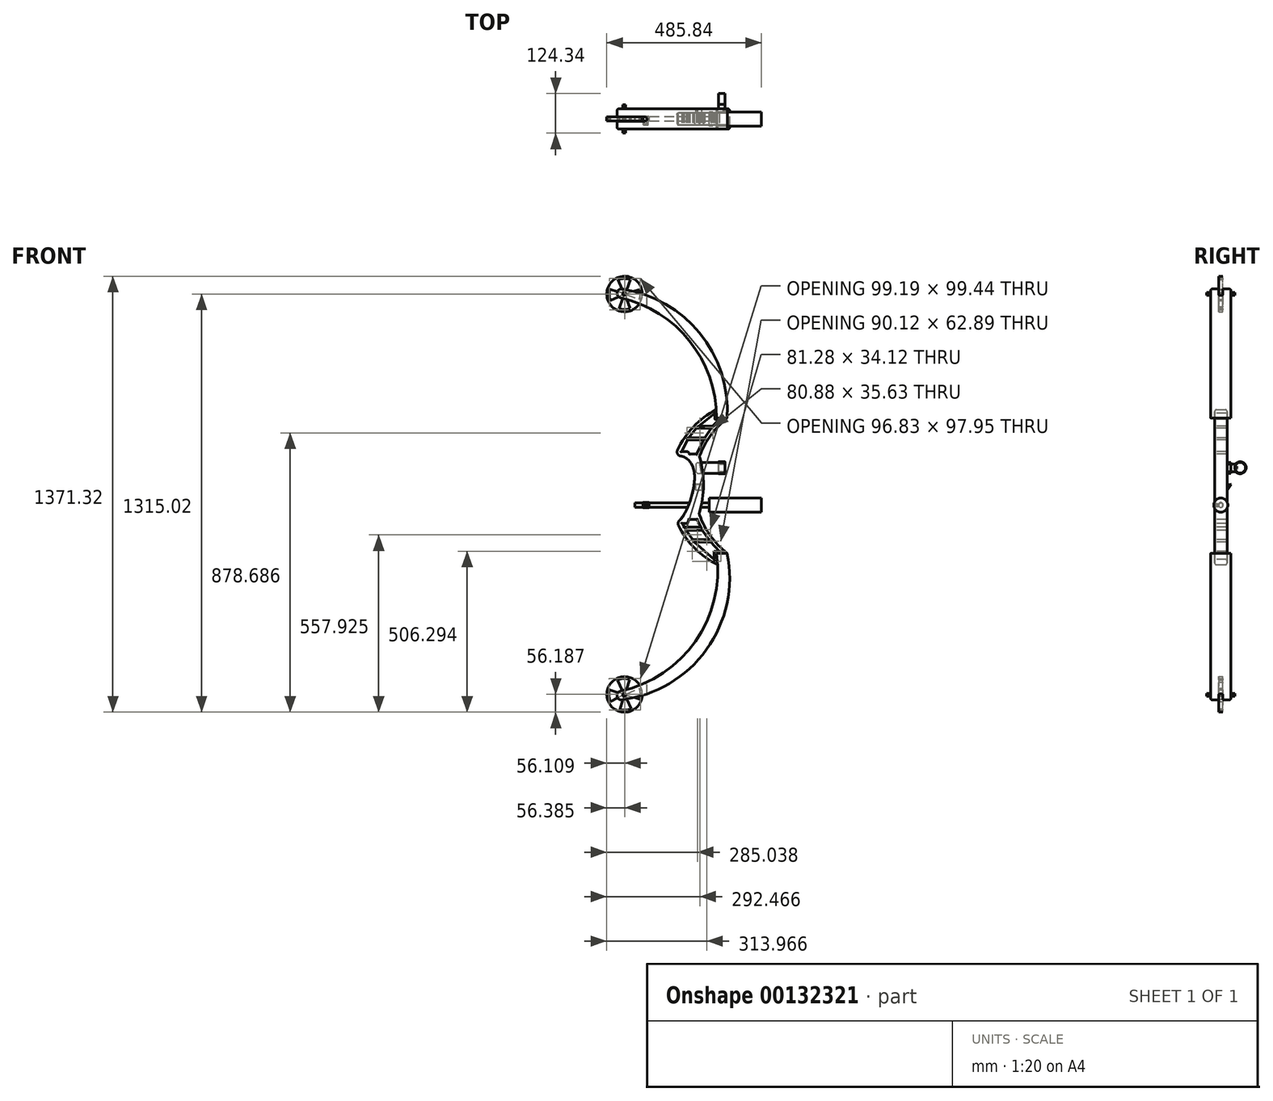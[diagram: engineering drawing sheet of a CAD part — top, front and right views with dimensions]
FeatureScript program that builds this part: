
annotation { "Feature Type Name" : "Feature", "Feature Type Description" : "" }
export const myFeature = defineFeature(function(context is Context, id is Id, definition is map)
    precondition{}
    {
        {
            var Q0;
            Q0=qCreatedBy(makeId("Front.planeOp"),FACE);
            var sketch = newSketch(context, id + "F0", { "sketchPlane" : qUnion([Q0])});
            skArc(sketch, "E0", {"start": v(312.15, 225.22) * mm, "mid": v(224.63, 471.96) * mm, "end": v(0, 606.44) * mm});
            skArc(sketch, "E1", {"start": v(0, -635.15) * mm, "mid": v(243.69, -480.2) * mm, "end": v(312.15, -199.65) * mm});
            skLineSegment(sketch, "E2", {"start": v(0, 606.44) * mm, "end": v(0, 633.37) * mm});
            skLineSegment(sketch, "E3", {"start": v(0, -635.15) * mm, "end": v(0, -662.07) * mm});
            skLineSegment(sketch, "E4", {"start": v(312.15, 225.22) * mm, "end": v(345.94, 225.22) * mm});
            skLineSegment(sketch, "E5", {"start": v(312.15, -199.65) * mm, "end": v(345.93, -199.65) * mm});
            skArc(sketch, "E6", {"start": v(345.94, 225.22) * mm, "mid": v(254.91, 498.75) * mm, "end": v(0, 633.37) * mm});
            skArc(sketch, "E7", {"start": v(0, -662.07) * mm, "mid": v(276.6, -508.4) * mm, "end": v(345.93, -199.65) * mm});
            skSolve(sketch);
        }
        {
            var Q0;
            Q0 = qSketchRegion(id + "F0", true);
            extrude(context, id + "F1", {"entities" : qUnion([Q0]), "depth" : 38.1 * mm, "hasSecondDirection" : true, "secondDirectionOppositeDirection" : true, "secondDirectionDepth" : 25.4 * mm});
        }
        {
            var Q0;
            Q0=qCreatedBy(makeId("Front.planeOp"),FACE);
            var sketch = newSketch(context, id + "F2", { "sketchPlane" : qUnion([Q0])});
            skArc(sketch, "E8", {"start": v(328.65, 260.2) * mm, "mid": v(164.15, 6.75) * mm, "end": v(333.35, -243.58) * mm});
            skArc(sketch, "E9", {"start": v(345.8, 225.54) * mm, "mid": v(242.77, 13.02) * mm, "end": v(345.76, -199.52) * mm});
            skLineSegment(sketch, "E10", {"start": v(333.35, -243.58) * mm, "end": v(345.76, -199.52) * mm});
            skLineSegment(sketch, "E11", {"start": v(328.65, 260.2) * mm, "end": v(345.8, 225.54) * mm});
            skArc(sketch, "E12", {"start": v(257.5, -75.1) * mm, "mid": v(271.65, 14.65) * mm, "end": v(258.73, 104.58) * mm});
            skArc(sketch, "E13", {"start": v(176.09, -70.66) * mm, "mid": v(193.2, 15.9) * mm, "end": v(180.78, 103.27) * mm});
            skSolve(sketch);
        }
        {
            var Q0;
            Q0 = qSketchRegion(id + "F2", true);
            extrude(context, id + "F3", {"entities" : qUnion([Q0]), "operationType" : NewBodyOperationType.ADD, "depth" : 25.4 * mm, "hasSecondDirection" : true, "secondDirectionOppositeDirection" : true, "secondDirectionDepth" : 13.4 * mm});
        }
        {
            var Q0;
            Q0 = qSketchRegion(id + "F2", true);
            extrude(context, id + "F4", {"entities" : qUnion([Q0]), "operationType" : NewBodyOperationType.ADD, "depth" : 25.4 * mm});
        }
        {
            var Q0;
            Q0=qCreatedBy(makeId("Front.planeOp"),FACE);
            var sketch = newSketch(context, id + "F5", { "sketchPlane" : qUnion([Q0])});
            skFitSpline(sketch, "E14", {"points": [v(182.57, 103.7) * mm, v(240.87, 63.55) * mm, v(188.22, -101.45) * mm, v(156.8, -24.45) * mm, v(182.57, 103.7) * mm]});
            skSolve(sketch);
        }
        {
            var Q0;
            Q0 = qSketchRegion(id + "F5", true);
            extrude(context, id + "F6", {"entities" : qUnion([Q0]), "operationType" : NewBodyOperationType.REMOVE, "oppositeDirection" : true, "depth" : 25.4 * mm, "hasSecondDirection" : true, "secondDirectionOppositeDirection" : false, "secondDirectionDepth" : 25.4 * mm});
        }
        {
            var Q0;
            {var subQ0=sQuery(id+"F2.wireOp",EDGE,"E8");Q0=makeQuery(id+"F6.boolean.opBoolean","INTERSECT",EDGE,{"disambiguationData":[OD(0.0)],"derivedFrom":[makeQuery(id+"F4.boolean.opBoolean","MERGE",FACE,{"derivedFrom":[makeQuery(id+"F3.opExtrude","SWEPT_FACE",FACE,{"disambiguationData":[OSD([subQ0])]}),makeQuery(id+"F4.opExtrude","SWEPT_FACE",FACE,{"disambiguationData":[OSD([subQ0])]})]}),makeQuery(id+"F6.opExtrude","SWEPT_FACE",FACE,{"disambiguationData":[OSD([sQuery(id+"F5.wireOp",EDGE,"E14")])]})]});}
            var Q1;
            {var subQ0=sQuery(id+"F2.wireOp",EDGE,"E8");Q1=makeQuery(id+"F6.boolean.opBoolean","INTERSECT",EDGE,{"disambiguationData":[OD(1.0)],"derivedFrom":[makeQuery(id+"F4.boolean.opBoolean","MERGE",FACE,{"derivedFrom":[makeQuery(id+"F3.opExtrude","SWEPT_FACE",FACE,{"disambiguationData":[OSD([subQ0])]}),makeQuery(id+"F4.opExtrude","SWEPT_FACE",FACE,{"disambiguationData":[OSD([subQ0])]})]}),makeQuery(id+"F6.opExtrude","SWEPT_FACE",FACE,{"disambiguationData":[OSD([sQuery(id+"F5.wireOp",EDGE,"E14")])]})]});}
            var Q2;
            {var subQ0=sQuery(id+"F2.wireOp",EDGE,"E12");var subQ1=sQuery(id+"F2.wireOp",EDGE,"E9");var subQ2=makeQuery(id+"F2.imprint","INTERSECT",VERTEX,{"disambiguationData":[OD(1.0)],"derivedFrom":[subQ1,subQ0]});Q2=makeQuery(id+"F4.boolean.opBoolean","MERGE",EDGE,{"derivedFrom":[makeQuery(id+"F3.opExtrude","SWEPT_EDGE",EDGE,{"disambiguationData":[OSD([subQ1,subQ0]),TDD([subQ2])]}),makeQuery(id+"F4.opExtrude","SWEPT_EDGE",EDGE,{"disambiguationData":[OSD([subQ1,subQ0]),TDD([subQ2])]})]});}
            var Q3;
            {var subQ0=sQuery(id+"F2.wireOp",EDGE,"E12");var subQ1=sQuery(id+"F2.wireOp",EDGE,"E9");var subQ2=makeQuery(id+"F2.imprint","INTERSECT",VERTEX,{"disambiguationData":[OD(0.0)],"derivedFrom":[subQ1,subQ0]});Q3=makeQuery(id+"F4.boolean.opBoolean","MERGE",EDGE,{"derivedFrom":[makeQuery(id+"F3.opExtrude","SWEPT_EDGE",EDGE,{"disambiguationData":[OSD([subQ1,subQ0]),TDD([subQ2])]}),makeQuery(id+"F4.opExtrude","SWEPT_EDGE",EDGE,{"disambiguationData":[OSD([subQ1,subQ0]),TDD([subQ2])]})]});}
            var Q4;
            Q4=makeQuery(id+"F1.opExtrude","SWEPT_EDGE",EDGE,{"disambiguationData":[OSD([sQuery(id+"F0.wireOp",EDGE,"E3"),sQuery(id+"F0.wireOp",EDGE,"E7")])]});
            var Q5;
            Q5=makeQuery(id+"F1.opExtrude","SWEPT_EDGE",EDGE,{"disambiguationData":[OSD([sQuery(id+"F0.wireOp",EDGE,"E1"),sQuery(id+"F0.wireOp",EDGE,"E3")])]});
            var Q6;
            Q6=makeQuery(id+"F1.opExtrude","SWEPT_EDGE",EDGE,{"disambiguationData":[OSD([sQuery(id+"F0.wireOp",EDGE,"E0"),sQuery(id+"F0.wireOp",EDGE,"E2")])]});
            var Q7;
            Q7=makeQuery(id+"F1.opExtrude","SWEPT_EDGE",EDGE,{"disambiguationData":[OSD([sQuery(id+"F0.wireOp",EDGE,"E2"),sQuery(id+"F0.wireOp",EDGE,"E6")])]});
            fillet(context, id + "F7", {"entities" : qUnion([Q0, Q1, Q2, Q3, Q4, Q5, Q6, Q7]), "radius" : 12.7 * mm, "tangentPropagation" : true, "allowEdgeOverflow" : false});
        }
        {
            var Q0;
            Q0=makeQuery(id+"F1.opExtrude","CAP_EDGE",EDGE,{"disambiguationData":[OSD([sQuery(id+"F0.wireOp",EDGE,"E0")])],"isStart":false});
            var Q1;
            Q1=makeQuery(id+"F1.opExtrude","CAP_EDGE",EDGE,{"disambiguationData":[OSD([sQuery(id+"F0.wireOp",EDGE,"E0")])],"isStart":true});
            var Q2;
            {var subQ0=sQuery(id+"F2.wireOp",EDGE,"E8");Q2=makeQuery(id+"F6.boolean.opBoolean","SPLIT",EDGE,{"disambiguationData":[TD([makeQuery(id+"F1.opExtrude","SWEPT_FACE",FACE,{"disambiguationData":[OSD([sQuery(id+"F0.wireOp",EDGE,"E0")])]})])],"derivedFrom":makeQuery(id+"F3.opExtrude","CAP_EDGE",EDGE,{"disambiguationData":[OSD([subQ0])],"isStart":true})});}
            var Q3;
            {var subQ0=sQuery(id+"F2.wireOp",EDGE,"E9");Q3=makeQuery(id+"F3.opExtrude","CAP_EDGE",EDGE,{"disambiguationData":[OSD([subQ0]),TDD([makeQuery(id+"F2.imprint","IMPRINT",EDGE,{"disambiguationData":[TD([[makeQuery(id+"F2.imprint","INTERSECT",VERTEX,{"derivedFrom":[subQ0,sQuery(id+"F2.wireOp",EDGE,"E11")]}),-1.0]])],"derivedFrom":subQ0})])],"isStart":true});}
            var Q4;
            {var subQ0=sQuery(id+"F2.wireOp",EDGE,"E8");Q4=makeQuery(id+"F6.boolean.opBoolean","SPLIT",EDGE,{"disambiguationData":[TD([makeQuery(id+"F1.opExtrude","SWEPT_FACE",FACE,{"disambiguationData":[OSD([sQuery(id+"F0.wireOp",EDGE,"E0")])]})])],"derivedFrom":makeQuery(id+"F3.opExtrude","CAP_EDGE",EDGE,{"disambiguationData":[OSD([subQ0])],"isStart":false})});}
            var Q5;
            {var subQ0=sQuery(id+"F2.wireOp",EDGE,"E9");Q5=makeQuery(id+"F3.opExtrude","CAP_EDGE",EDGE,{"disambiguationData":[OSD([subQ0]),TDD([makeQuery(id+"F2.imprint","IMPRINT",EDGE,{"disambiguationData":[TD([[makeQuery(id+"F2.imprint","INTERSECT",VERTEX,{"derivedFrom":[subQ0,sQuery(id+"F2.wireOp",EDGE,"E11")]}),-1.0]])],"derivedFrom":subQ0})])],"isStart":false});}
            var Q6;
            Q6=makeQuery(id+"F1.opExtrude","CAP_EDGE",EDGE,{"disambiguationData":[OSD([sQuery(id+"F0.wireOp",EDGE,"E1")])],"isStart":true});
            var Q7;
            Q7=makeQuery(id+"F1.opExtrude","CAP_EDGE",EDGE,{"disambiguationData":[OSD([sQuery(id+"F0.wireOp",EDGE,"E1")])],"isStart":false});
            fillet(context, id + "F8", {"entities" : qUnion([Q0, Q1, Q2, Q3, Q4, Q5, Q6, Q7]), "radius" : 5.08 * mm, "tangentPropagation" : true, "allowEdgeOverflow" : false});
        }
        {
            var Q0;
            Q0=qCreatedBy(makeId("Top.planeOp"),FACE);
            var sketch = newSketch(context, id + "F9", { "sketchPlane" : qUnion([Q0])});
            skLineSegment(sketch, "E15", {"start": v(0, 0) * mm, "end": v(87.64, 0) * mm});
            skLineSegment(sketch, "E16", {"start": v(0, -12.95) * mm, "end": v(87.64, -12.95) * mm});
            skArc(sketch, "E17", {"start": v(87.64, -12.95) * mm, "mid": v(94.11, -6.48) * mm, "end": v(87.64, 0) * mm});
            skLineSegment(sketch, "E18", {"start": v(0, 0) * mm, "end": v(0, -12.95) * mm});
            skSolve(sketch);
        }
        {
            var Q0;
            Q0 = qSketchRegion(id + "F9", true);
            extrude(context, id + "F10", {"entities" : qUnion([Q0]), "operationType" : NewBodyOperationType.REMOVE, "oppositeDirection" : true, "depth" : 1043.23 * mm, "hasSecondDirection" : true, "secondDirectionOppositeDirection" : false, "secondDirectionDepth" : 725.43 * mm});
        }
        {
            var Q0;
            Q0=qCreatedBy(makeId("Front.planeOp"),FACE);
            var sketch = newSketch(context, id + "F11", { "sketchPlane" : qUnion([Q0])});
            skLineSegment(sketch, "E19", {"start": v(307.3, 240.65) * mm, "end": v(307.3, 221.5) * mm});
            skLineSegment(sketch, "E20", {"start": v(307.3, 221.5) * mm, "end": v(321.6, 221.5) * mm});
            skLineSegment(sketch, "E21", {"start": v(321.6, 221.5) * mm, "end": v(299.17, 200.17) * mm});
            skLineSegment(sketch, "E22", {"start": v(299.17, 200.17) * mm, "end": v(257.15, 200.17) * mm});
            skLineSegment(sketch, "E23", {"start": v(257.15, 200.17) * mm, "end": v(307.3, 240.65) * mm});
            skLineSegment(sketch, "E24", {"start": v(249.41, 194.56) * mm, "end": v(295.62, 194.56) * mm});
            skLineSegment(sketch, "E25", {"start": v(295.62, 194.56) * mm, "end": v(275.44, 164.01) * mm});
            skLineSegment(sketch, "E26", {"start": v(275.44, 164.01) * mm, "end": v(224.78, 164.01) * mm});
            skLineSegment(sketch, "E27", {"start": v(224.78, 164.01) * mm, "end": v(249.41, 194.56) * mm});
            skLineSegment(sketch, "E28", {"start": v(221.45, 157.23) * mm, "end": v(202.6, 120.92) * mm});
            skLineSegment(sketch, "E29", {"start": v(202.6, 120.92) * mm, "end": v(222.32, 120.92) * mm});
            skLineSegment(sketch, "E30", {"start": v(222.32, 120.92) * mm, "end": v(228.43, 112.54) * mm});
            skLineSegment(sketch, "E31", {"start": v(228.43, 112.54) * mm, "end": v(249.56, 112.54) * mm});
            skLineSegment(sketch, "E32", {"start": v(249.56, 112.54) * mm, "end": v(272.08, 156.7) * mm});
            skLineSegment(sketch, "E33", {"start": v(272.08, 156.7) * mm, "end": v(221.45, 157.23) * mm});
            skSolve(sketch);
        }
        {
            var Q0;
            Q0 = qSketchRegion(id + "F11", true);
            extrude(context, id + "F12", {"entities" : qUnion([Q0]), "operationType" : NewBodyOperationType.REMOVE, "oppositeDirection" : true, "depth" : 25.4 * mm, "hasSecondDirection" : true, "secondDirectionOppositeDirection" : false, "secondDirectionDepth" : 103.34 * mm});
        }
        {
            var Q0;
            Q0=qCreatedBy(makeId("Front.planeOp"),FACE);
            var sketch = newSketch(context, id + "F13", { "sketchPlane" : qUnion([Q0])});
            skLineSegment(sketch, "E34", {"start": v(304.9, -218.91) * mm, "end": v(304.9, -193.2) * mm});
            skLineSegment(sketch, "E35", {"start": v(304.9, -193.2) * mm, "end": v(320.72, -193.2) * mm});
            skLineSegment(sketch, "E36", {"start": v(320.72, -193.2) * mm, "end": v(294.36, -164.2) * mm});
            skLineSegment(sketch, "E37", {"start": v(294.36, -164.2) * mm, "end": v(243.05, -164.2) * mm});
            skLineSegment(sketch, "E38", {"start": v(243.05, -164.2) * mm, "end": v(304.9, -218.91) * mm});
            skLineSegment(sketch, "E39", {"start": v(288.23, -156) * mm, "end": v(237.22, -156) * mm});
            skLineSegment(sketch, "E40", {"start": v(237.22, -156) * mm, "end": v(216.74, -126.96) * mm});
            skLineSegment(sketch, "E41", {"start": v(216.74, -126.96) * mm, "end": v(267.82, -126.96) * mm});
            skLineSegment(sketch, "E42", {"start": v(267.82, -126.96) * mm, "end": v(288.23, -156) * mm});
            skLineSegment(sketch, "E43", {"start": v(262.27, -117.14) * mm, "end": v(210.93, -117.14) * mm});
            skLineSegment(sketch, "E44", {"start": v(210.93, -117.14) * mm, "end": v(205.44, -106.16) * mm});
            skLineSegment(sketch, "E45", {"start": v(205.44, -106.16) * mm, "end": v(220.33, -106.16) * mm});
            skLineSegment(sketch, "E46", {"start": v(220.33, -106.16) * mm, "end": v(226.6, -93.23) * mm});
            skLineSegment(sketch, "E47", {"start": v(226.6, -93.23) * mm, "end": v(251.3, -93.23) * mm});
            skLineSegment(sketch, "E48", {"start": v(251.3, -93.23) * mm, "end": v(262.27, -117.14) * mm});
            skSolve(sketch);
        }
        {
            var Q0;
            Q0 = qSketchRegion(id + "F13", true);
            extrude(context, id + "F14", {"entities" : qUnion([Q0]), "operationType" : NewBodyOperationType.REMOVE, "oppositeDirection" : true, "depth" : 25.4 * mm, "hasSecondDirection" : true, "secondDirectionOppositeDirection" : false, "secondDirectionDepth" : 136.26 * mm});
        }
        {
            var Q0;
            Q0=qCreatedBy(makeId("Front.planeOp"),FACE);
            var sketch = newSketch(context, id + "F15", { "sketchPlane" : qUnion([Q0])});
            skCircle(sketch, "E49", {"center": v(23.33, 616.03) * mm, "radius": 55.9 * mm});
            skCircle(sketch, "E50", {"center": v(23.33, -643.5) * mm, "radius": 55.9 * mm});
            skCircle(sketch, "E51", {"center": v(23.33, 616.03) * mm, "radius": 4.58 * mm});
            skLineSegment(sketch, "E52", {"start": v(19.88, 619.04) * mm, "end": v(2.06, 661.07) * mm});
            skLineSegment(sketch, "E53", {"start": v(26.37, 619.46) * mm, "end": v(42.28, 661.63) * mm});
            skLineSegment(sketch, "E54", {"start": v(20.5, 612.42) * mm, "end": v(6.51, 570.45) * mm});
            skLineSegment(sketch, "E55", {"start": v(26.38, 612.6) * mm, "end": v(40.24, 570.82) * mm});
            skArc(sketch, "E56", {"start": v(42.28, 661.63) * mm, "mid": v(22.13, 664.6) * mm, "end": v(2.06, 661.07) * mm});
            skArc(sketch, "E57", {"start": v(6.51, 570.45) * mm, "mid": v(23.42, 566.64) * mm, "end": v(40.24, 570.82) * mm});
            skLineSegment(sketch, "E58", {"start": v(27.5, 617.94) * mm, "end": v(69.87, 630.2) * mm});
            skLineSegment(sketch, "E59", {"start": v(27.5, 614.11) * mm, "end": v(69.21, 598.67) * mm});
            skLineSegment(sketch, "E60", {"start": v(19.14, 617.87) * mm, "end": v(-22.68, 630.88) * mm});
            skLineSegment(sketch, "E61", {"start": v(19.1, 614.26) * mm, "end": v(-21.29, 595.17) * mm});
            skArc(sketch, "E62", {"start": v(-22.68, 630.88) * mm, "mid": v(-24.57, 612.92) * mm, "end": v(-21.29, 595.17) * mm});
            skArc(sketch, "E63", {"start": v(69.21, 598.67) * mm, "mid": v(72.24, 614.38) * mm, "end": v(69.87, 630.2) * mm});
            skCircle(sketch, "E64", {"center": v(23.33, -643.5) * mm, "radius": 4.58 * mm});
            skLineSegment(sketch, "E65", {"start": v(20.29, -640.08) * mm, "end": v(1.41, -598.57) * mm});
            skLineSegment(sketch, "E66", {"start": v(25.93, -639.73) * mm, "end": v(39.75, -596.96) * mm});
            skLineSegment(sketch, "E67", {"start": v(21.54, -647.73) * mm, "end": v(8.9, -690.96) * mm});
            skLineSegment(sketch, "E68", {"start": v(26, -647.23) * mm, "end": v(44, -688.73) * mm});
            skLineSegment(sketch, "E69", {"start": v(27.8, -642.46) * mm, "end": v(69.69, -624.26) * mm});
            skLineSegment(sketch, "E70", {"start": v(27.47, -645.49) * mm, "end": v(70.34, -658.33) * mm});
            skLineSegment(sketch, "E71", {"start": v(18.96, -642.13) * mm, "end": v(-24.47, -629.13) * mm});
            skLineSegment(sketch, "E72", {"start": v(19.17, -645.42) * mm, "end": v(-19.95, -665.33) * mm});
            skArc(sketch, "E73", {"start": v(39.75, -596.96) * mm, "mid": v(20.4, -593.5) * mm, "end": v(1.41, -598.57) * mm});
            skArc(sketch, "E74", {"start": v(-24.47, -629.13) * mm, "mid": v(-25.69, -647.66) * mm, "end": v(-19.95, -665.33) * mm});
            skArc(sketch, "E75", {"start": v(8.9, -690.96) * mm, "mid": v(26.64, -692.84) * mm, "end": v(44, -688.73) * mm});
            skArc(sketch, "E76", {"start": v(70.34, -658.33) * mm, "mid": v(73.15, -641.24) * mm, "end": v(69.69, -624.26) * mm});
            skSolve(sketch);
        }
        {
            var Q0;
            Q0=qCreatedBy(makeId("Front.planeOp"),FACE);
            var sketch = newSketch(context, id + "F16", { "sketchPlane" : qUnion([Q0])});
            skCircle(sketch, "E77", {"center": v(21.85, 616.5) * mm, "radius": 4.59 * mm});
            skCircle(sketch, "E78", {"center": v(21.85, -645.2) * mm, "radius": 4.58 * mm});
            skSolve(sketch);
        }
        {
            var Q0;
            Q0 = qSketchRegion(id + "F16", true);
            extrude(context, id + "F17", {"entities" : qUnion([Q0]), "operationType" : NewBodyOperationType.ADD, "depth" : 50.8 * mm, "hasSecondDirection" : true, "secondDirectionOppositeDirection" : true, "secondDirectionDepth" : 38.1 * mm});
        }
        {
            var Q0;
            Q0 = qSketchRegion(id + "F15", true);
            extrude(context, id + "F18", {"entities" : qUnion([Q0]), "depth" : 12.7 * mm});
        }
        {
            var Q0;
            Q0=makeQuery(id+"F12.boolean.opBoolean","INTERSECT",EDGE,{"derivedFrom":[makeQuery(id+"F3.opExtrude","CAP_FACE",FACE,{"disambiguationData":[OSD([sQuery(id+"F2.wireOp",EDGE,"E8"),sQuery(id+"F2.wireOp",EDGE,"E9"),sQuery(id+"F2.wireOp",EDGE,"E10"),sQuery(id+"F2.wireOp",EDGE,"E11"),sQuery(id+"F2.wireOp",EDGE,"E12")])],"isStart":false}),makeQuery(id+"F12.opExtrude","SWEPT_FACE",FACE,{"disambiguationData":[OSD([sQuery(id+"F11.wireOp",EDGE,"E26")])]})]});
            var Q1;
            Q1=makeQuery(id+"F12.boolean.opBoolean","INTERSECT",EDGE,{"derivedFrom":[makeQuery(id+"F3.opExtrude","CAP_FACE",FACE,{"disambiguationData":[OSD([sQuery(id+"F2.wireOp",EDGE,"E8"),sQuery(id+"F2.wireOp",EDGE,"E9"),sQuery(id+"F2.wireOp",EDGE,"E10"),sQuery(id+"F2.wireOp",EDGE,"E11"),sQuery(id+"F2.wireOp",EDGE,"E12")])],"isStart":false}),makeQuery(id+"F12.opExtrude","SWEPT_FACE",FACE,{"disambiguationData":[OSD([sQuery(id+"F11.wireOp",EDGE,"E31")])]})]});
            var Q2;
            Q2=makeQuery(id+"F12.boolean.opBoolean","INTERSECT",EDGE,{"derivedFrom":[makeQuery(id+"F3.opExtrude","CAP_FACE",FACE,{"disambiguationData":[OSD([sQuery(id+"F2.wireOp",EDGE,"E8"),sQuery(id+"F2.wireOp",EDGE,"E9"),sQuery(id+"F2.wireOp",EDGE,"E10"),sQuery(id+"F2.wireOp",EDGE,"E11"),sQuery(id+"F2.wireOp",EDGE,"E12")])],"isStart":false}),makeQuery(id+"F12.opExtrude","SWEPT_FACE",FACE,{"disambiguationData":[OSD([sQuery(id+"F11.wireOp",EDGE,"E30")])]})]});
            var Q3;
            Q3=makeQuery(id+"F12.boolean.opBoolean","INTERSECT",EDGE,{"derivedFrom":[makeQuery(id+"F3.opExtrude","CAP_FACE",FACE,{"disambiguationData":[OSD([sQuery(id+"F2.wireOp",EDGE,"E8"),sQuery(id+"F2.wireOp",EDGE,"E9"),sQuery(id+"F2.wireOp",EDGE,"E10"),sQuery(id+"F2.wireOp",EDGE,"E11"),sQuery(id+"F2.wireOp",EDGE,"E12")])],"isStart":false}),makeQuery(id+"F12.opExtrude","SWEPT_FACE",FACE,{"disambiguationData":[OSD([sQuery(id+"F11.wireOp",EDGE,"E29")])]})]});
            var Q4;
            Q4=makeQuery(id+"F12.boolean.opBoolean","INTERSECT",EDGE,{"derivedFrom":[makeQuery(id+"F3.opExtrude","CAP_FACE",FACE,{"disambiguationData":[OSD([sQuery(id+"F2.wireOp",EDGE,"E8"),sQuery(id+"F2.wireOp",EDGE,"E9"),sQuery(id+"F2.wireOp",EDGE,"E10"),sQuery(id+"F2.wireOp",EDGE,"E11"),sQuery(id+"F2.wireOp",EDGE,"E12")])],"isStart":false}),makeQuery(id+"F12.opExtrude","SWEPT_FACE",FACE,{"disambiguationData":[OSD([sQuery(id+"F11.wireOp",EDGE,"E32")])]})]});
            var Q5;
            Q5=makeQuery(id+"F12.boolean.opBoolean","INTERSECT",EDGE,{"derivedFrom":[makeQuery(id+"F3.opExtrude","CAP_FACE",FACE,{"disambiguationData":[OSD([sQuery(id+"F2.wireOp",EDGE,"E8"),sQuery(id+"F2.wireOp",EDGE,"E9"),sQuery(id+"F2.wireOp",EDGE,"E10"),sQuery(id+"F2.wireOp",EDGE,"E11"),sQuery(id+"F2.wireOp",EDGE,"E12")])],"isStart":false}),makeQuery(id+"F12.opExtrude","SWEPT_FACE",FACE,{"disambiguationData":[OSD([sQuery(id+"F11.wireOp",EDGE,"E33")])]})]});
            var Q6;
            Q6=makeQuery(id+"F12.boolean.opBoolean","INTERSECT",EDGE,{"derivedFrom":[makeQuery(id+"F3.opExtrude","CAP_FACE",FACE,{"disambiguationData":[OSD([sQuery(id+"F2.wireOp",EDGE,"E8"),sQuery(id+"F2.wireOp",EDGE,"E9"),sQuery(id+"F2.wireOp",EDGE,"E10"),sQuery(id+"F2.wireOp",EDGE,"E11"),sQuery(id+"F2.wireOp",EDGE,"E12")])],"isStart":false}),makeQuery(id+"F12.opExtrude","SWEPT_FACE",FACE,{"disambiguationData":[OSD([sQuery(id+"F11.wireOp",EDGE,"E28")])]})]});
            var Q7;
            Q7=makeQuery(id+"F12.boolean.opBoolean","INTERSECT",EDGE,{"derivedFrom":[makeQuery(id+"F3.opExtrude","CAP_FACE",FACE,{"disambiguationData":[OSD([sQuery(id+"F2.wireOp",EDGE,"E8"),sQuery(id+"F2.wireOp",EDGE,"E9"),sQuery(id+"F2.wireOp",EDGE,"E10"),sQuery(id+"F2.wireOp",EDGE,"E11"),sQuery(id+"F2.wireOp",EDGE,"E12")])],"isStart":false}),makeQuery(id+"F12.opExtrude","SWEPT_FACE",FACE,{"disambiguationData":[OSD([sQuery(id+"F11.wireOp",EDGE,"E25")])]})]});
            var Q8;
            Q8=makeQuery(id+"F12.boolean.opBoolean","INTERSECT",EDGE,{"derivedFrom":[makeQuery(id+"F3.opExtrude","CAP_FACE",FACE,{"disambiguationData":[OSD([sQuery(id+"F2.wireOp",EDGE,"E8"),sQuery(id+"F2.wireOp",EDGE,"E9"),sQuery(id+"F2.wireOp",EDGE,"E10"),sQuery(id+"F2.wireOp",EDGE,"E11"),sQuery(id+"F2.wireOp",EDGE,"E12")])],"isStart":false}),makeQuery(id+"F12.opExtrude","SWEPT_FACE",FACE,{"disambiguationData":[OSD([sQuery(id+"F11.wireOp",EDGE,"E24")])]})]});
            var Q9;
            Q9=makeQuery(id+"F12.boolean.opBoolean","INTERSECT",EDGE,{"derivedFrom":[makeQuery(id+"F3.opExtrude","CAP_FACE",FACE,{"disambiguationData":[OSD([sQuery(id+"F2.wireOp",EDGE,"E8"),sQuery(id+"F2.wireOp",EDGE,"E9"),sQuery(id+"F2.wireOp",EDGE,"E10"),sQuery(id+"F2.wireOp",EDGE,"E11"),sQuery(id+"F2.wireOp",EDGE,"E12")])],"isStart":false}),makeQuery(id+"F12.opExtrude","SWEPT_FACE",FACE,{"disambiguationData":[OSD([sQuery(id+"F11.wireOp",EDGE,"E27")])]})]});
            var Q10;
            Q10=makeQuery(id+"F12.boolean.opBoolean","INTERSECT",EDGE,{"derivedFrom":[makeQuery(id+"F3.opExtrude","CAP_FACE",FACE,{"disambiguationData":[OSD([sQuery(id+"F2.wireOp",EDGE,"E8"),sQuery(id+"F2.wireOp",EDGE,"E9"),sQuery(id+"F2.wireOp",EDGE,"E10"),sQuery(id+"F2.wireOp",EDGE,"E11"),sQuery(id+"F2.wireOp",EDGE,"E12")])],"isStart":false}),makeQuery(id+"F12.opExtrude","SWEPT_FACE",FACE,{"disambiguationData":[OSD([sQuery(id+"F11.wireOp",EDGE,"E22")])]})]});
            var Q11;
            Q11=makeQuery(id+"F12.boolean.opBoolean","INTERSECT",EDGE,{"derivedFrom":[makeQuery(id+"F3.opExtrude","CAP_FACE",FACE,{"disambiguationData":[OSD([sQuery(id+"F2.wireOp",EDGE,"E8"),sQuery(id+"F2.wireOp",EDGE,"E9"),sQuery(id+"F2.wireOp",EDGE,"E10"),sQuery(id+"F2.wireOp",EDGE,"E11"),sQuery(id+"F2.wireOp",EDGE,"E12")])],"isStart":false}),makeQuery(id+"F12.opExtrude","SWEPT_FACE",FACE,{"disambiguationData":[OSD([sQuery(id+"F11.wireOp",EDGE,"E21")])]})]});
            var Q12;
            Q12=makeQuery(id+"F12.boolean.opBoolean","INTERSECT",EDGE,{"derivedFrom":[makeQuery(id+"F3.opExtrude","CAP_FACE",FACE,{"disambiguationData":[OSD([sQuery(id+"F2.wireOp",EDGE,"E8"),sQuery(id+"F2.wireOp",EDGE,"E9"),sQuery(id+"F2.wireOp",EDGE,"E10"),sQuery(id+"F2.wireOp",EDGE,"E11"),sQuery(id+"F2.wireOp",EDGE,"E12")])],"isStart":false}),makeQuery(id+"F12.opExtrude","SWEPT_FACE",FACE,{"disambiguationData":[OSD([sQuery(id+"F11.wireOp",EDGE,"E20")])]})]});
            var Q13;
            Q13=makeQuery(id+"F12.boolean.opBoolean","INTERSECT",EDGE,{"derivedFrom":[makeQuery(id+"F3.opExtrude","CAP_FACE",FACE,{"disambiguationData":[OSD([sQuery(id+"F2.wireOp",EDGE,"E8"),sQuery(id+"F2.wireOp",EDGE,"E9"),sQuery(id+"F2.wireOp",EDGE,"E10"),sQuery(id+"F2.wireOp",EDGE,"E11"),sQuery(id+"F2.wireOp",EDGE,"E12")])],"isStart":false}),makeQuery(id+"F12.opExtrude","SWEPT_FACE",FACE,{"disambiguationData":[OSD([sQuery(id+"F11.wireOp",EDGE,"E19")])]})]});
            var Q14;
            Q14=makeQuery(id+"F12.boolean.opBoolean","INTERSECT",EDGE,{"derivedFrom":[makeQuery(id+"F3.opExtrude","CAP_FACE",FACE,{"disambiguationData":[OSD([sQuery(id+"F2.wireOp",EDGE,"E8"),sQuery(id+"F2.wireOp",EDGE,"E9"),sQuery(id+"F2.wireOp",EDGE,"E10"),sQuery(id+"F2.wireOp",EDGE,"E11"),sQuery(id+"F2.wireOp",EDGE,"E12")])],"isStart":false}),makeQuery(id+"F12.opExtrude","SWEPT_FACE",FACE,{"disambiguationData":[OSD([sQuery(id+"F11.wireOp",EDGE,"E23")])]})]});
            var Q15;
            Q15=makeQuery(id+"F12.boolean.opBoolean","INTERSECT",EDGE,{"derivedFrom":[makeQuery(id+"F3.opExtrude","CAP_FACE",FACE,{"disambiguationData":[OSD([sQuery(id+"F2.wireOp",EDGE,"E8"),sQuery(id+"F2.wireOp",EDGE,"E9"),sQuery(id+"F2.wireOp",EDGE,"E10"),sQuery(id+"F2.wireOp",EDGE,"E11"),sQuery(id+"F2.wireOp",EDGE,"E12")])],"isStart":true}),makeQuery(id+"F12.opExtrude","SWEPT_FACE",FACE,{"disambiguationData":[OSD([sQuery(id+"F11.wireOp",EDGE,"E31")])]})]});
            var Q16;
            Q16=makeQuery(id+"F12.boolean.opBoolean","INTERSECT",EDGE,{"derivedFrom":[makeQuery(id+"F3.opExtrude","CAP_FACE",FACE,{"disambiguationData":[OSD([sQuery(id+"F2.wireOp",EDGE,"E8"),sQuery(id+"F2.wireOp",EDGE,"E9"),sQuery(id+"F2.wireOp",EDGE,"E10"),sQuery(id+"F2.wireOp",EDGE,"E11"),sQuery(id+"F2.wireOp",EDGE,"E12")])],"isStart":true}),makeQuery(id+"F12.opExtrude","SWEPT_FACE",FACE,{"disambiguationData":[OSD([sQuery(id+"F11.wireOp",EDGE,"E30")])]})]});
            var Q17;
            Q17=makeQuery(id+"F12.boolean.opBoolean","INTERSECT",EDGE,{"derivedFrom":[makeQuery(id+"F3.opExtrude","CAP_FACE",FACE,{"disambiguationData":[OSD([sQuery(id+"F2.wireOp",EDGE,"E8"),sQuery(id+"F2.wireOp",EDGE,"E9"),sQuery(id+"F2.wireOp",EDGE,"E10"),sQuery(id+"F2.wireOp",EDGE,"E11"),sQuery(id+"F2.wireOp",EDGE,"E12")])],"isStart":true}),makeQuery(id+"F12.opExtrude","SWEPT_FACE",FACE,{"disambiguationData":[OSD([sQuery(id+"F11.wireOp",EDGE,"E29")])]})]});
            var Q18;
            Q18=makeQuery(id+"F12.boolean.opBoolean","INTERSECT",EDGE,{"derivedFrom":[makeQuery(id+"F3.opExtrude","CAP_FACE",FACE,{"disambiguationData":[OSD([sQuery(id+"F2.wireOp",EDGE,"E8"),sQuery(id+"F2.wireOp",EDGE,"E9"),sQuery(id+"F2.wireOp",EDGE,"E10"),sQuery(id+"F2.wireOp",EDGE,"E11"),sQuery(id+"F2.wireOp",EDGE,"E12")])],"isStart":true}),makeQuery(id+"F12.opExtrude","SWEPT_FACE",FACE,{"disambiguationData":[OSD([sQuery(id+"F11.wireOp",EDGE,"E28")])]})]});
            var Q19;
            Q19=makeQuery(id+"F12.boolean.opBoolean","INTERSECT",EDGE,{"derivedFrom":[makeQuery(id+"F3.opExtrude","CAP_FACE",FACE,{"disambiguationData":[OSD([sQuery(id+"F2.wireOp",EDGE,"E8"),sQuery(id+"F2.wireOp",EDGE,"E9"),sQuery(id+"F2.wireOp",EDGE,"E10"),sQuery(id+"F2.wireOp",EDGE,"E11"),sQuery(id+"F2.wireOp",EDGE,"E12")])],"isStart":true}),makeQuery(id+"F12.opExtrude","SWEPT_FACE",FACE,{"disambiguationData":[OSD([sQuery(id+"F11.wireOp",EDGE,"E33")])]})]});
            var Q20;
            Q20=makeQuery(id+"F12.boolean.opBoolean","INTERSECT",EDGE,{"derivedFrom":[makeQuery(id+"F3.opExtrude","CAP_FACE",FACE,{"disambiguationData":[OSD([sQuery(id+"F2.wireOp",EDGE,"E8"),sQuery(id+"F2.wireOp",EDGE,"E9"),sQuery(id+"F2.wireOp",EDGE,"E10"),sQuery(id+"F2.wireOp",EDGE,"E11"),sQuery(id+"F2.wireOp",EDGE,"E12")])],"isStart":true}),makeQuery(id+"F12.opExtrude","SWEPT_FACE",FACE,{"disambiguationData":[OSD([sQuery(id+"F11.wireOp",EDGE,"E32")])]})]});
            var Q21;
            Q21=makeQuery(id+"F12.boolean.opBoolean","INTERSECT",EDGE,{"derivedFrom":[makeQuery(id+"F3.opExtrude","CAP_FACE",FACE,{"disambiguationData":[OSD([sQuery(id+"F2.wireOp",EDGE,"E8"),sQuery(id+"F2.wireOp",EDGE,"E9"),sQuery(id+"F2.wireOp",EDGE,"E10"),sQuery(id+"F2.wireOp",EDGE,"E11"),sQuery(id+"F2.wireOp",EDGE,"E12")])],"isStart":true}),makeQuery(id+"F12.opExtrude","SWEPT_FACE",FACE,{"disambiguationData":[OSD([sQuery(id+"F11.wireOp",EDGE,"E25")])]})]});
            var Q22;
            Q22=makeQuery(id+"F12.boolean.opBoolean","INTERSECT",EDGE,{"derivedFrom":[makeQuery(id+"F3.opExtrude","CAP_FACE",FACE,{"disambiguationData":[OSD([sQuery(id+"F2.wireOp",EDGE,"E8"),sQuery(id+"F2.wireOp",EDGE,"E9"),sQuery(id+"F2.wireOp",EDGE,"E10"),sQuery(id+"F2.wireOp",EDGE,"E11"),sQuery(id+"F2.wireOp",EDGE,"E12")])],"isStart":true}),makeQuery(id+"F12.opExtrude","SWEPT_FACE",FACE,{"disambiguationData":[OSD([sQuery(id+"F11.wireOp",EDGE,"E26")])]})]});
            var Q23;
            Q23=makeQuery(id+"F12.boolean.opBoolean","INTERSECT",EDGE,{"derivedFrom":[makeQuery(id+"F3.opExtrude","CAP_FACE",FACE,{"disambiguationData":[OSD([sQuery(id+"F2.wireOp",EDGE,"E8"),sQuery(id+"F2.wireOp",EDGE,"E9"),sQuery(id+"F2.wireOp",EDGE,"E10"),sQuery(id+"F2.wireOp",EDGE,"E11"),sQuery(id+"F2.wireOp",EDGE,"E12")])],"isStart":true}),makeQuery(id+"F12.opExtrude","SWEPT_FACE",FACE,{"disambiguationData":[OSD([sQuery(id+"F11.wireOp",EDGE,"E27")])]})]});
            var Q24;
            Q24=makeQuery(id+"F12.boolean.opBoolean","INTERSECT",EDGE,{"derivedFrom":[makeQuery(id+"F3.opExtrude","CAP_FACE",FACE,{"disambiguationData":[OSD([sQuery(id+"F2.wireOp",EDGE,"E8"),sQuery(id+"F2.wireOp",EDGE,"E9"),sQuery(id+"F2.wireOp",EDGE,"E10"),sQuery(id+"F2.wireOp",EDGE,"E11"),sQuery(id+"F2.wireOp",EDGE,"E12")])],"isStart":true}),makeQuery(id+"F12.opExtrude","SWEPT_FACE",FACE,{"disambiguationData":[OSD([sQuery(id+"F11.wireOp",EDGE,"E24")])]})]});
            var Q25;
            Q25=makeQuery(id+"F12.boolean.opBoolean","INTERSECT",EDGE,{"derivedFrom":[makeQuery(id+"F3.opExtrude","CAP_FACE",FACE,{"disambiguationData":[OSD([sQuery(id+"F2.wireOp",EDGE,"E8"),sQuery(id+"F2.wireOp",EDGE,"E9"),sQuery(id+"F2.wireOp",EDGE,"E10"),sQuery(id+"F2.wireOp",EDGE,"E11"),sQuery(id+"F2.wireOp",EDGE,"E12")])],"isStart":true}),makeQuery(id+"F12.opExtrude","SWEPT_FACE",FACE,{"disambiguationData":[OSD([sQuery(id+"F11.wireOp",EDGE,"E22")])]})]});
            var Q26;
            Q26=makeQuery(id+"F12.boolean.opBoolean","INTERSECT",EDGE,{"derivedFrom":[makeQuery(id+"F3.opExtrude","CAP_FACE",FACE,{"disambiguationData":[OSD([sQuery(id+"F2.wireOp",EDGE,"E8"),sQuery(id+"F2.wireOp",EDGE,"E9"),sQuery(id+"F2.wireOp",EDGE,"E10"),sQuery(id+"F2.wireOp",EDGE,"E11"),sQuery(id+"F2.wireOp",EDGE,"E12")])],"isStart":true}),makeQuery(id+"F12.opExtrude","SWEPT_FACE",FACE,{"disambiguationData":[OSD([sQuery(id+"F11.wireOp",EDGE,"E21")])]})]});
            var Q27;
            Q27=makeQuery(id+"F12.boolean.opBoolean","INTERSECT",EDGE,{"derivedFrom":[makeQuery(id+"F3.opExtrude","CAP_FACE",FACE,{"disambiguationData":[OSD([sQuery(id+"F2.wireOp",EDGE,"E8"),sQuery(id+"F2.wireOp",EDGE,"E9"),sQuery(id+"F2.wireOp",EDGE,"E10"),sQuery(id+"F2.wireOp",EDGE,"E11"),sQuery(id+"F2.wireOp",EDGE,"E12")])],"isStart":true}),makeQuery(id+"F12.opExtrude","SWEPT_FACE",FACE,{"disambiguationData":[OSD([sQuery(id+"F11.wireOp",EDGE,"E23")])]})]});
            var Q28;
            Q28=makeQuery(id+"F12.boolean.opBoolean","INTERSECT",EDGE,{"derivedFrom":[makeQuery(id+"F3.opExtrude","CAP_FACE",FACE,{"disambiguationData":[OSD([sQuery(id+"F2.wireOp",EDGE,"E8"),sQuery(id+"F2.wireOp",EDGE,"E9"),sQuery(id+"F2.wireOp",EDGE,"E10"),sQuery(id+"F2.wireOp",EDGE,"E11"),sQuery(id+"F2.wireOp",EDGE,"E12")])],"isStart":true}),makeQuery(id+"F12.opExtrude","SWEPT_FACE",FACE,{"disambiguationData":[OSD([sQuery(id+"F11.wireOp",EDGE,"E20")])]})]});
            var Q29;
            Q29=makeQuery(id+"F12.boolean.opBoolean","INTERSECT",EDGE,{"derivedFrom":[makeQuery(id+"F3.opExtrude","CAP_FACE",FACE,{"disambiguationData":[OSD([sQuery(id+"F2.wireOp",EDGE,"E8"),sQuery(id+"F2.wireOp",EDGE,"E9"),sQuery(id+"F2.wireOp",EDGE,"E10"),sQuery(id+"F2.wireOp",EDGE,"E11"),sQuery(id+"F2.wireOp",EDGE,"E12")])],"isStart":true}),makeQuery(id+"F12.opExtrude","SWEPT_FACE",FACE,{"disambiguationData":[OSD([sQuery(id+"F11.wireOp",EDGE,"E19")])]})]});
            fillet(context, id + "F19", {"entities" : qUnion([Q0, Q1, Q2, Q3, Q4, Q5, Q6, Q7, Q8, Q9, Q10, Q11, Q12, Q13, Q14, Q15, Q16, Q17, Q18, Q19, Q20, Q21, Q22, Q23, Q24, Q25, Q26, Q27, Q28, Q29]), "radius" : 2.54 * mm, "tangentPropagation" : true, "allowEdgeOverflow" : false});
        }
        {
            var Q0;
            Q0=makeQuery(id+"F14.boolean.opBoolean","INTERSECT",EDGE,{"derivedFrom":[makeQuery(id+"F3.opExtrude","CAP_FACE",FACE,{"disambiguationData":[OSD([sQuery(id+"F2.wireOp",EDGE,"E8"),sQuery(id+"F2.wireOp",EDGE,"E9"),sQuery(id+"F2.wireOp",EDGE,"E10"),sQuery(id+"F2.wireOp",EDGE,"E11"),sQuery(id+"F2.wireOp",EDGE,"E12")])],"isStart":true}),makeQuery(id+"F14.opExtrude","SWEPT_FACE",FACE,{"disambiguationData":[OSD([sQuery(id+"F13.wireOp",EDGE,"E47")])]})]});
            var Q1;
            Q1=makeQuery(id+"F14.boolean.opBoolean","INTERSECT",EDGE,{"derivedFrom":[makeQuery(id+"F3.opExtrude","CAP_FACE",FACE,{"disambiguationData":[OSD([sQuery(id+"F2.wireOp",EDGE,"E8"),sQuery(id+"F2.wireOp",EDGE,"E9"),sQuery(id+"F2.wireOp",EDGE,"E10"),sQuery(id+"F2.wireOp",EDGE,"E11"),sQuery(id+"F2.wireOp",EDGE,"E12")])],"isStart":true}),makeQuery(id+"F14.opExtrude","SWEPT_FACE",FACE,{"disambiguationData":[OSD([sQuery(id+"F13.wireOp",EDGE,"E46")])]})]});
            var Q2;
            Q2=makeQuery(id+"F14.boolean.opBoolean","INTERSECT",EDGE,{"derivedFrom":[makeQuery(id+"F3.opExtrude","CAP_FACE",FACE,{"disambiguationData":[OSD([sQuery(id+"F2.wireOp",EDGE,"E8"),sQuery(id+"F2.wireOp",EDGE,"E9"),sQuery(id+"F2.wireOp",EDGE,"E10"),sQuery(id+"F2.wireOp",EDGE,"E11"),sQuery(id+"F2.wireOp",EDGE,"E12")])],"isStart":true}),makeQuery(id+"F14.opExtrude","SWEPT_FACE",FACE,{"disambiguationData":[OSD([sQuery(id+"F13.wireOp",EDGE,"E45")])]})]});
            var Q3;
            Q3=makeQuery(id+"F14.boolean.opBoolean","INTERSECT",EDGE,{"derivedFrom":[makeQuery(id+"F3.opExtrude","CAP_FACE",FACE,{"disambiguationData":[OSD([sQuery(id+"F2.wireOp",EDGE,"E8"),sQuery(id+"F2.wireOp",EDGE,"E9"),sQuery(id+"F2.wireOp",EDGE,"E10"),sQuery(id+"F2.wireOp",EDGE,"E11"),sQuery(id+"F2.wireOp",EDGE,"E12")])],"isStart":true}),makeQuery(id+"F14.opExtrude","SWEPT_FACE",FACE,{"disambiguationData":[OSD([sQuery(id+"F13.wireOp",EDGE,"E44")])]})]});
            var Q4;
            Q4=makeQuery(id+"F14.boolean.opBoolean","INTERSECT",EDGE,{"derivedFrom":[makeQuery(id+"F3.opExtrude","CAP_FACE",FACE,{"disambiguationData":[OSD([sQuery(id+"F2.wireOp",EDGE,"E8"),sQuery(id+"F2.wireOp",EDGE,"E9"),sQuery(id+"F2.wireOp",EDGE,"E10"),sQuery(id+"F2.wireOp",EDGE,"E11"),sQuery(id+"F2.wireOp",EDGE,"E12")])],"isStart":true}),makeQuery(id+"F14.opExtrude","SWEPT_FACE",FACE,{"disambiguationData":[OSD([sQuery(id+"F13.wireOp",EDGE,"E43")])]})]});
            var Q5;
            Q5=makeQuery(id+"F14.boolean.opBoolean","INTERSECT",EDGE,{"derivedFrom":[makeQuery(id+"F3.opExtrude","CAP_FACE",FACE,{"disambiguationData":[OSD([sQuery(id+"F2.wireOp",EDGE,"E8"),sQuery(id+"F2.wireOp",EDGE,"E9"),sQuery(id+"F2.wireOp",EDGE,"E10"),sQuery(id+"F2.wireOp",EDGE,"E11"),sQuery(id+"F2.wireOp",EDGE,"E12")])],"isStart":false}),makeQuery(id+"F14.opExtrude","SWEPT_FACE",FACE,{"disambiguationData":[OSD([sQuery(id+"F13.wireOp",EDGE,"E48")])]})]});
            var Q6;
            Q6=makeQuery(id+"F14.boolean.opBoolean","INTERSECT",EDGE,{"derivedFrom":[makeQuery(id+"F3.opExtrude","CAP_FACE",FACE,{"disambiguationData":[OSD([sQuery(id+"F2.wireOp",EDGE,"E8"),sQuery(id+"F2.wireOp",EDGE,"E9"),sQuery(id+"F2.wireOp",EDGE,"E10"),sQuery(id+"F2.wireOp",EDGE,"E11"),sQuery(id+"F2.wireOp",EDGE,"E12")])],"isStart":true}),makeQuery(id+"F14.opExtrude","SWEPT_FACE",FACE,{"disambiguationData":[OSD([sQuery(id+"F13.wireOp",EDGE,"E48")])]})]});
            var Q7;
            Q7=makeQuery(id+"F14.boolean.opBoolean","INTERSECT",EDGE,{"derivedFrom":[makeQuery(id+"F3.opExtrude","CAP_FACE",FACE,{"disambiguationData":[OSD([sQuery(id+"F2.wireOp",EDGE,"E8"),sQuery(id+"F2.wireOp",EDGE,"E9"),sQuery(id+"F2.wireOp",EDGE,"E10"),sQuery(id+"F2.wireOp",EDGE,"E11"),sQuery(id+"F2.wireOp",EDGE,"E12")])],"isStart":true}),makeQuery(id+"F14.opExtrude","SWEPT_FACE",FACE,{"disambiguationData":[OSD([sQuery(id+"F13.wireOp",EDGE,"E41")])]})]});
            var Q8;
            Q8=makeQuery(id+"F14.boolean.opBoolean","INTERSECT",EDGE,{"derivedFrom":[makeQuery(id+"F3.opExtrude","CAP_FACE",FACE,{"disambiguationData":[OSD([sQuery(id+"F2.wireOp",EDGE,"E8"),sQuery(id+"F2.wireOp",EDGE,"E9"),sQuery(id+"F2.wireOp",EDGE,"E10"),sQuery(id+"F2.wireOp",EDGE,"E11"),sQuery(id+"F2.wireOp",EDGE,"E12")])],"isStart":true}),makeQuery(id+"F14.opExtrude","SWEPT_FACE",FACE,{"disambiguationData":[OSD([sQuery(id+"F13.wireOp",EDGE,"E40")])]})]});
            var Q9;
            Q9=makeQuery(id+"F14.boolean.opBoolean","INTERSECT",EDGE,{"derivedFrom":[makeQuery(id+"F3.opExtrude","CAP_FACE",FACE,{"disambiguationData":[OSD([sQuery(id+"F2.wireOp",EDGE,"E8"),sQuery(id+"F2.wireOp",EDGE,"E9"),sQuery(id+"F2.wireOp",EDGE,"E10"),sQuery(id+"F2.wireOp",EDGE,"E11"),sQuery(id+"F2.wireOp",EDGE,"E12")])],"isStart":true}),makeQuery(id+"F14.opExtrude","SWEPT_FACE",FACE,{"disambiguationData":[OSD([sQuery(id+"F13.wireOp",EDGE,"E39")])]})]});
            var Q10;
            Q10=makeQuery(id+"F14.boolean.opBoolean","INTERSECT",EDGE,{"derivedFrom":[makeQuery(id+"F3.opExtrude","CAP_FACE",FACE,{"disambiguationData":[OSD([sQuery(id+"F2.wireOp",EDGE,"E8"),sQuery(id+"F2.wireOp",EDGE,"E9"),sQuery(id+"F2.wireOp",EDGE,"E10"),sQuery(id+"F2.wireOp",EDGE,"E11"),sQuery(id+"F2.wireOp",EDGE,"E12")])],"isStart":true}),makeQuery(id+"F14.opExtrude","SWEPT_FACE",FACE,{"disambiguationData":[OSD([sQuery(id+"F13.wireOp",EDGE,"E42")])]})]});
            var Q11;
            Q11=makeQuery(id+"F14.boolean.opBoolean","INTERSECT",EDGE,{"derivedFrom":[makeQuery(id+"F3.opExtrude","CAP_FACE",FACE,{"disambiguationData":[OSD([sQuery(id+"F2.wireOp",EDGE,"E8"),sQuery(id+"F2.wireOp",EDGE,"E9"),sQuery(id+"F2.wireOp",EDGE,"E10"),sQuery(id+"F2.wireOp",EDGE,"E11"),sQuery(id+"F2.wireOp",EDGE,"E12")])],"isStart":false}),makeQuery(id+"F14.opExtrude","SWEPT_FACE",FACE,{"disambiguationData":[OSD([sQuery(id+"F13.wireOp",EDGE,"E42")])]})]});
            var Q12;
            Q12=makeQuery(id+"F14.boolean.opBoolean","INTERSECT",EDGE,{"derivedFrom":[makeQuery(id+"F3.opExtrude","CAP_FACE",FACE,{"disambiguationData":[OSD([sQuery(id+"F2.wireOp",EDGE,"E8"),sQuery(id+"F2.wireOp",EDGE,"E9"),sQuery(id+"F2.wireOp",EDGE,"E10"),sQuery(id+"F2.wireOp",EDGE,"E11"),sQuery(id+"F2.wireOp",EDGE,"E12")])],"isStart":false}),makeQuery(id+"F14.opExtrude","SWEPT_FACE",FACE,{"disambiguationData":[OSD([sQuery(id+"F13.wireOp",EDGE,"E40")])]})]});
            var Q13;
            Q13=makeQuery(id+"F14.boolean.opBoolean","INTERSECT",EDGE,{"derivedFrom":[makeQuery(id+"F3.opExtrude","CAP_FACE",FACE,{"disambiguationData":[OSD([sQuery(id+"F2.wireOp",EDGE,"E8"),sQuery(id+"F2.wireOp",EDGE,"E9"),sQuery(id+"F2.wireOp",EDGE,"E10"),sQuery(id+"F2.wireOp",EDGE,"E11"),sQuery(id+"F2.wireOp",EDGE,"E12")])],"isStart":false}),makeQuery(id+"F14.opExtrude","SWEPT_FACE",FACE,{"disambiguationData":[OSD([sQuery(id+"F13.wireOp",EDGE,"E39")])]})]});
            var Q14;
            Q14=makeQuery(id+"F14.boolean.opBoolean","INTERSECT",EDGE,{"derivedFrom":[makeQuery(id+"F3.opExtrude","CAP_FACE",FACE,{"disambiguationData":[OSD([sQuery(id+"F2.wireOp",EDGE,"E8"),sQuery(id+"F2.wireOp",EDGE,"E9"),sQuery(id+"F2.wireOp",EDGE,"E10"),sQuery(id+"F2.wireOp",EDGE,"E11"),sQuery(id+"F2.wireOp",EDGE,"E12")])],"isStart":false}),makeQuery(id+"F14.opExtrude","SWEPT_FACE",FACE,{"disambiguationData":[OSD([sQuery(id+"F13.wireOp",EDGE,"E41")])]})]});
            var Q15;
            Q15=makeQuery(id+"F14.boolean.opBoolean","INTERSECT",EDGE,{"derivedFrom":[makeQuery(id+"F3.opExtrude","CAP_FACE",FACE,{"disambiguationData":[OSD([sQuery(id+"F2.wireOp",EDGE,"E8"),sQuery(id+"F2.wireOp",EDGE,"E9"),sQuery(id+"F2.wireOp",EDGE,"E10"),sQuery(id+"F2.wireOp",EDGE,"E11"),sQuery(id+"F2.wireOp",EDGE,"E12")])],"isStart":true}),makeQuery(id+"F14.opExtrude","SWEPT_FACE",FACE,{"disambiguationData":[OSD([sQuery(id+"F13.wireOp",EDGE,"E38")])]})]});
            var Q16;
            Q16=makeQuery(id+"F14.boolean.opBoolean","INTERSECT",EDGE,{"derivedFrom":[makeQuery(id+"F3.opExtrude","CAP_FACE",FACE,{"disambiguationData":[OSD([sQuery(id+"F2.wireOp",EDGE,"E8"),sQuery(id+"F2.wireOp",EDGE,"E9"),sQuery(id+"F2.wireOp",EDGE,"E10"),sQuery(id+"F2.wireOp",EDGE,"E11"),sQuery(id+"F2.wireOp",EDGE,"E12")])],"isStart":true}),makeQuery(id+"F14.opExtrude","SWEPT_FACE",FACE,{"disambiguationData":[OSD([sQuery(id+"F13.wireOp",EDGE,"E37")])]})]});
            var Q17;
            Q17=makeQuery(id+"F14.boolean.opBoolean","INTERSECT",EDGE,{"derivedFrom":[makeQuery(id+"F3.opExtrude","CAP_FACE",FACE,{"disambiguationData":[OSD([sQuery(id+"F2.wireOp",EDGE,"E8"),sQuery(id+"F2.wireOp",EDGE,"E9"),sQuery(id+"F2.wireOp",EDGE,"E10"),sQuery(id+"F2.wireOp",EDGE,"E11"),sQuery(id+"F2.wireOp",EDGE,"E12")])],"isStart":true}),makeQuery(id+"F14.opExtrude","SWEPT_FACE",FACE,{"disambiguationData":[OSD([sQuery(id+"F13.wireOp",EDGE,"E36")])]})]});
            var Q18;
            Q18=makeQuery(id+"F14.boolean.opBoolean","INTERSECT",EDGE,{"derivedFrom":[makeQuery(id+"F3.opExtrude","CAP_FACE",FACE,{"disambiguationData":[OSD([sQuery(id+"F2.wireOp",EDGE,"E8"),sQuery(id+"F2.wireOp",EDGE,"E9"),sQuery(id+"F2.wireOp",EDGE,"E10"),sQuery(id+"F2.wireOp",EDGE,"E11"),sQuery(id+"F2.wireOp",EDGE,"E12")])],"isStart":true}),makeQuery(id+"F14.opExtrude","SWEPT_FACE",FACE,{"disambiguationData":[OSD([sQuery(id+"F13.wireOp",EDGE,"E35")])]})]});
            var Q19;
            Q19=makeQuery(id+"F14.boolean.opBoolean","INTERSECT",EDGE,{"derivedFrom":[makeQuery(id+"F3.opExtrude","CAP_FACE",FACE,{"disambiguationData":[OSD([sQuery(id+"F2.wireOp",EDGE,"E8"),sQuery(id+"F2.wireOp",EDGE,"E9"),sQuery(id+"F2.wireOp",EDGE,"E10"),sQuery(id+"F2.wireOp",EDGE,"E11"),sQuery(id+"F2.wireOp",EDGE,"E12")])],"isStart":true}),makeQuery(id+"F14.opExtrude","SWEPT_FACE",FACE,{"disambiguationData":[OSD([sQuery(id+"F13.wireOp",EDGE,"E34")])]})]});
            var Q20;
            Q20=makeQuery(id+"F14.boolean.opBoolean","INTERSECT",EDGE,{"derivedFrom":[makeQuery(id+"F3.opExtrude","CAP_FACE",FACE,{"disambiguationData":[OSD([sQuery(id+"F2.wireOp",EDGE,"E8"),sQuery(id+"F2.wireOp",EDGE,"E9"),sQuery(id+"F2.wireOp",EDGE,"E10"),sQuery(id+"F2.wireOp",EDGE,"E11"),sQuery(id+"F2.wireOp",EDGE,"E12")])],"isStart":false}),makeQuery(id+"F14.opExtrude","SWEPT_FACE",FACE,{"disambiguationData":[OSD([sQuery(id+"F13.wireOp",EDGE,"E43")])]})]});
            var Q21;
            Q21=makeQuery(id+"F14.boolean.opBoolean","INTERSECT",EDGE,{"derivedFrom":[makeQuery(id+"F3.opExtrude","CAP_FACE",FACE,{"disambiguationData":[OSD([sQuery(id+"F2.wireOp",EDGE,"E8"),sQuery(id+"F2.wireOp",EDGE,"E9"),sQuery(id+"F2.wireOp",EDGE,"E10"),sQuery(id+"F2.wireOp",EDGE,"E11"),sQuery(id+"F2.wireOp",EDGE,"E12")])],"isStart":false}),makeQuery(id+"F14.opExtrude","SWEPT_FACE",FACE,{"disambiguationData":[OSD([sQuery(id+"F13.wireOp",EDGE,"E44")])]})]});
            var Q22;
            Q22=makeQuery(id+"F14.boolean.opBoolean","INTERSECT",EDGE,{"derivedFrom":[makeQuery(id+"F3.opExtrude","CAP_FACE",FACE,{"disambiguationData":[OSD([sQuery(id+"F2.wireOp",EDGE,"E8"),sQuery(id+"F2.wireOp",EDGE,"E9"),sQuery(id+"F2.wireOp",EDGE,"E10"),sQuery(id+"F2.wireOp",EDGE,"E11"),sQuery(id+"F2.wireOp",EDGE,"E12")])],"isStart":false}),makeQuery(id+"F14.opExtrude","SWEPT_FACE",FACE,{"disambiguationData":[OSD([sQuery(id+"F13.wireOp",EDGE,"E45")])]})]});
            var Q23;
            Q23=makeQuery(id+"F14.boolean.opBoolean","INTERSECT",EDGE,{"derivedFrom":[makeQuery(id+"F3.opExtrude","CAP_FACE",FACE,{"disambiguationData":[OSD([sQuery(id+"F2.wireOp",EDGE,"E8"),sQuery(id+"F2.wireOp",EDGE,"E9"),sQuery(id+"F2.wireOp",EDGE,"E10"),sQuery(id+"F2.wireOp",EDGE,"E11"),sQuery(id+"F2.wireOp",EDGE,"E12")])],"isStart":false}),makeQuery(id+"F14.opExtrude","SWEPT_FACE",FACE,{"disambiguationData":[OSD([sQuery(id+"F13.wireOp",EDGE,"E46")])]})]});
            var Q24;
            Q24=makeQuery(id+"F14.boolean.opBoolean","INTERSECT",EDGE,{"derivedFrom":[makeQuery(id+"F3.opExtrude","CAP_FACE",FACE,{"disambiguationData":[OSD([sQuery(id+"F2.wireOp",EDGE,"E8"),sQuery(id+"F2.wireOp",EDGE,"E9"),sQuery(id+"F2.wireOp",EDGE,"E10"),sQuery(id+"F2.wireOp",EDGE,"E11"),sQuery(id+"F2.wireOp",EDGE,"E12")])],"isStart":false}),makeQuery(id+"F14.opExtrude","SWEPT_FACE",FACE,{"disambiguationData":[OSD([sQuery(id+"F13.wireOp",EDGE,"E47")])]})]});
            var Q25;
            Q25=makeQuery(id+"F14.boolean.opBoolean","INTERSECT",EDGE,{"derivedFrom":[makeQuery(id+"F3.opExtrude","CAP_FACE",FACE,{"disambiguationData":[OSD([sQuery(id+"F2.wireOp",EDGE,"E8"),sQuery(id+"F2.wireOp",EDGE,"E9"),sQuery(id+"F2.wireOp",EDGE,"E10"),sQuery(id+"F2.wireOp",EDGE,"E11"),sQuery(id+"F2.wireOp",EDGE,"E12")])],"isStart":false}),makeQuery(id+"F14.opExtrude","SWEPT_FACE",FACE,{"disambiguationData":[OSD([sQuery(id+"F13.wireOp",EDGE,"E38")])]})]});
            var Q26;
            Q26=makeQuery(id+"F14.boolean.opBoolean","INTERSECT",EDGE,{"derivedFrom":[makeQuery(id+"F3.opExtrude","CAP_FACE",FACE,{"disambiguationData":[OSD([sQuery(id+"F2.wireOp",EDGE,"E8"),sQuery(id+"F2.wireOp",EDGE,"E9"),sQuery(id+"F2.wireOp",EDGE,"E10"),sQuery(id+"F2.wireOp",EDGE,"E11"),sQuery(id+"F2.wireOp",EDGE,"E12")])],"isStart":false}),makeQuery(id+"F14.opExtrude","SWEPT_FACE",FACE,{"disambiguationData":[OSD([sQuery(id+"F13.wireOp",EDGE,"E37")])]})]});
            var Q27;
            Q27=makeQuery(id+"F14.boolean.opBoolean","INTERSECT",EDGE,{"derivedFrom":[makeQuery(id+"F3.opExtrude","CAP_FACE",FACE,{"disambiguationData":[OSD([sQuery(id+"F2.wireOp",EDGE,"E8"),sQuery(id+"F2.wireOp",EDGE,"E9"),sQuery(id+"F2.wireOp",EDGE,"E10"),sQuery(id+"F2.wireOp",EDGE,"E11"),sQuery(id+"F2.wireOp",EDGE,"E12")])],"isStart":false}),makeQuery(id+"F14.opExtrude","SWEPT_FACE",FACE,{"disambiguationData":[OSD([sQuery(id+"F13.wireOp",EDGE,"E36")])]})]});
            var Q28;
            Q28=makeQuery(id+"F14.boolean.opBoolean","INTERSECT",EDGE,{"derivedFrom":[makeQuery(id+"F3.opExtrude","CAP_FACE",FACE,{"disambiguationData":[OSD([sQuery(id+"F2.wireOp",EDGE,"E8"),sQuery(id+"F2.wireOp",EDGE,"E9"),sQuery(id+"F2.wireOp",EDGE,"E10"),sQuery(id+"F2.wireOp",EDGE,"E11"),sQuery(id+"F2.wireOp",EDGE,"E12")])],"isStart":false}),makeQuery(id+"F14.opExtrude","SWEPT_FACE",FACE,{"disambiguationData":[OSD([sQuery(id+"F13.wireOp",EDGE,"E34")])]})]});
            var Q29;
            Q29=makeQuery(id+"F14.boolean.opBoolean","INTERSECT",EDGE,{"derivedFrom":[makeQuery(id+"F3.opExtrude","CAP_FACE",FACE,{"disambiguationData":[OSD([sQuery(id+"F2.wireOp",EDGE,"E8"),sQuery(id+"F2.wireOp",EDGE,"E9"),sQuery(id+"F2.wireOp",EDGE,"E10"),sQuery(id+"F2.wireOp",EDGE,"E11"),sQuery(id+"F2.wireOp",EDGE,"E12")])],"isStart":false}),makeQuery(id+"F14.opExtrude","SWEPT_FACE",FACE,{"disambiguationData":[OSD([sQuery(id+"F13.wireOp",EDGE,"E35")])]})]});
            fillet(context, id + "F20", {"entities" : qUnion([Q0, Q1, Q2, Q3, Q4, Q5, Q6, Q7, Q8, Q9, Q10, Q11, Q12, Q13, Q14, Q15, Q16, Q17, Q18, Q19, Q20, Q21, Q22, Q23, Q24, Q25, Q26, Q27, Q28, Q29]), "radius" : 2.54 * mm, "tangentPropagation" : true, "allowEdgeOverflow" : false});
        }
        {
            var Q0;
            Q0=qCreatedBy(makeId("Right.planeOp"),FACE);
            var sketch = newSketch(context, id + "F21", { "sketchPlane" : qUnion([Q0])});
            skCircle(sketch, "E79", {"center": v(-6.32, -48.15) * mm, "radius": 6.8 * mm});
            skSolve(sketch);
        }
        {
            var Q0;
            Q0 = qSketchRegion(id + "F21", true);
            extrude(context, id + "F22", {"entities" : qUnion([Q0]), "operationType" : NewBodyOperationType.ADD, "depth" : 427.88 * mm, "hasSecondDirection" : true, "secondDirectionOppositeDirection" : false, "secondDirectionDepth" : 55.16 * mm});
        }
        {
            var Q0;
            Q0=makeQuery(id+"F22.opExtrude","CAP_FACE",FACE,{"disambiguationData":[OSD([sQuery(id+"F21.wireOp",EDGE,"E79")])],"isStart":false});
            var sketch = newSketch(context, id + "F23", { "sketchPlane" : qUnion([Q0])});
            skCircle(sketch, "E80", {"center": v(-6.32, -48.15) * mm, "radius": 22.23 * mm});
            skSolve(sketch);
        }
        {
            var Q0;
            Q0 = qSketchRegion(id + "F23", true);
            extrude(context, id + "F24", {"entities" : qUnion([Q0]), "operationType" : NewBodyOperationType.ADD, "depth" : 25.4 * mm, "hasSecondDirection" : true, "secondDirectionOppositeDirection" : true, "secondDirectionDepth" : 138.2 * mm});
        }
        {
            var Q0;
            Q0=makeQuery(id+"F3.opExtrude","CAP_FACE",FACE,{"disambiguationData":[OSD([sQuery(id+"F2.wireOp",EDGE,"E8"),sQuery(id+"F2.wireOp",EDGE,"E9"),sQuery(id+"F2.wireOp",EDGE,"E10"),sQuery(id+"F2.wireOp",EDGE,"E11"),sQuery(id+"F2.wireOp",EDGE,"E12")])],"isStart":true});
            var sketch = newSketch(context, id + "F25", { "sketchPlane" : qUnion([Q0])});
            skLineSegment(sketch, "E81.bottom", {"start": v(-248.02, 86.34) * mm, "end": v(-338.98, 86.34) * mm});
            skLineSegment(sketch, "E81.top", {"start": v(-248.02, 52.26) * mm, "end": v(-338.98, 52.26) * mm});
            skLineSegment(sketch, "E81.left", {"start": v(-248.02, 86.34) * mm, "end": v(-248.02, 52.26) * mm});
            skLineSegment(sketch, "E81.right", {"start": v(-338.98, 86.34) * mm, "end": v(-338.98, 52.26) * mm});
            skSolve(sketch);
        }
        {
            var Q0;
            Q0 = qSketchRegion(id + "F25", true);
            extrude(context, id + "F26", {"entities" : qUnion([Q0]), "operationType" : NewBodyOperationType.ADD, "depth" : 12.3 * mm});
        }
        {
            var Q0;
            Q0=makeQuery(id+"F26.opExtrude","SWEPT_EDGE",EDGE,{"disambiguationData":[OSD([sQuery(id+"F25.wireOp",EDGE,"E81.bottom"),sQuery(id+"F25.wireOp",EDGE,"E81.right")])]});
            var Q1;
            Q1=makeQuery(id+"F26.opExtrude","SWEPT_EDGE",EDGE,{"disambiguationData":[OSD([sQuery(id+"F25.wireOp",EDGE,"E81.top"),sQuery(id+"F25.wireOp",EDGE,"E81.right")])]});
            chamfer(context, id + "F27", {"entities" : qUnion([Q0, Q1]), "width" : 5.08 * mm, "tangentPropagation" : true});
        }
        {
            var Q0;
            Q0=qCreatedBy(makeId("Right.planeOp"),FACE);
            var sketch = newSketch(context, id + "F28", { "sketchPlane" : qUnion([Q0])});
            skCircle(sketch, "E82", {"center": v(54.58, 69.49) * mm, "radius": 18.96 * mm});
            skLineSegment(sketch, "E83", {"start": v(25.53, 81.36) * mm, "end": v(39.8, 81.36) * mm});
            skLineSegment(sketch, "E84", {"start": v(25.53, 57.22) * mm, "end": v(40.12, 57.22) * mm});
            skLineSegment(sketch, "E85", {"start": v(25.53, 81.36) * mm, "end": v(25.53, 57.22) * mm});
            skCircle(sketch, "E86", {"center": v(54.58, 69.49) * mm, "radius": 16.75 * mm});
            skSolve(sketch);
        }
        {
            var Q0;
            Q0 = qSketchRegion(id + "F28", true);
            extrude(context, id + "F29", {"entities" : qUnion([Q0]), "operationType" : NewBodyOperationType.ADD, "depth" : 339.09 * mm, "hasSecondDirection" : true, "secondDirectionOppositeDirection" : false, "secondDirectionDepth" : 318.24 * mm});
        }
        {
            var Q0;
            Q0=qCreatedBy(makeId("Right.planeOp"),FACE);
            var sketch = newSketch(context, id + "F30", { "sketchPlane" : qUnion([Q0])});
            skLineSegment(sketch, "E87", {"start": v(38.18, 73.29) * mm, "end": v(43.84, 73.29) * mm});
            skLineSegment(sketch, "E88", {"start": v(43.84, 73.29) * mm, "end": v(43.84, 72.1) * mm});
            skLineSegment(sketch, "E89", {"start": v(43.84, 72.1) * mm, "end": v(37.72, 72.1) * mm});
            skLineSegment(sketch, "E90", {"start": v(37.72, 70.47) * mm, "end": v(43.74, 70.47) * mm});
            skLineSegment(sketch, "E91", {"start": v(43.74, 70.47) * mm, "end": v(43.74, 69.13) * mm});
            skLineSegment(sketch, "E92", {"start": v(43.74, 69.13) * mm, "end": v(36.88, 69.13) * mm});
            skLineSegment(sketch, "E93", {"start": v(36.88, 69.13) * mm, "end": v(37.72, 70.47) * mm});
            skLineSegment(sketch, "E94", {"start": v(37.72, 72.1) * mm, "end": v(38.18, 73.29) * mm});
            skLineSegment(sketch, "E95", {"start": v(37.6, 67.54) * mm, "end": v(43.64, 67.54) * mm});
            skLineSegment(sketch, "E96", {"start": v(43.64, 67.54) * mm, "end": v(43.64, 66.24) * mm});
            skLineSegment(sketch, "E97", {"start": v(43.64, 66.24) * mm, "end": v(37.5, 66.24) * mm});
            skLineSegment(sketch, "E98", {"start": v(37.5, 66.24) * mm, "end": v(37.6, 67.54) * mm});
            skSolve(sketch);
        }
        {
            var Q0;
            Q0 = qSketchRegion(id + "F30", true);
            extrude(context, id + "F31", {"entities" : qUnion([Q0]), "depth" : 339.02 * mm, "hasSecondDirection" : true, "secondDirectionOppositeDirection" : false, "secondDirectionDepth" : 338.24 * mm});
        }
        {
            var Q0;
            Q0=makeQuery(id+"F26.opExtrude","SWEPT_EDGE",EDGE,{"disambiguationData":[OSD([sQuery(id+"F25.wireOp",EDGE,"E81.bottom"),sQuery(id+"F25.wireOp",EDGE,"E81.left")])]});
            var Q1;
            Q1=makeQuery(id+"F26.opExtrude","SWEPT_EDGE",EDGE,{"disambiguationData":[OSD([sQuery(id+"F25.wireOp",EDGE,"E81.top"),sQuery(id+"F25.wireOp",EDGE,"E81.left")])]});
            chamfer(context, id + "F32", {"entities" : qUnion([Q0, Q1]), "width" : 5.08 * mm, "tangentPropagation" : true});
        }
        {
            var Q0;
            Q0=qCreatedBy(makeId("Front.planeOp"),FACE);
            var sketch = newSketch(context, id + "F33", { "sketchPlane" : qUnion([Q0])});
            skLineSegment(sketch, "E99", {"start": v(-32.72, 618.44) * mm, "end": v(-32.72, -645.7) * mm});
            skLineSegment(sketch, "E100.0", {"start": v(-31.12, 618.44) * mm, "end": v(-31.12, -645.7) * mm});
            skSolve(sketch);
        }
        {
            var Q0;
            Q0=sQuery(id+"F33.wireOp",EDGE,"E100.0");
            var Q1;
            Q1=sQuery(id+"F33.wireOp",EDGE,"E99");
            revolve(context, id + "F34", {"bodyType" : ToolBodyType.SURFACE, "surfaceEntities" : qUnion([Q0]), "axis" : qUnion([Q1]), "revolveType" : RevolveType.FULL});
        }
        {
            var Q0;
            Q0=makeQuery(id+"F22.opExtrude","CAP_FACE",FACE,{"disambiguationData":[OSD([sQuery(id+"F21.wireOp",EDGE,"E79")])],"isStart":true});
            var sketch = newSketch(context, id + "F35", { "sketchPlane" : qUnion([Q0])});
            skCircle(sketch, "E101", {"center": v(6.32, -48.15) * mm, "radius": 7.8 * mm});
            skSolve(sketch);
        }
        {
            var Q0;
            Q0=makeQuery(id+"F35.imprint","IMPRINT",FACE,{"disambiguationData":[TD([[makeQuery(id+"F35.imprint","IMPRINT",EDGE,{"derivedFrom":sQuery(id+"F35.wireOp",EDGE,"E101")}),1.0]])]});
            extrude(context, id + "F36", {"entities" : qUnion([Q0]), "operationType" : NewBodyOperationType.ADD, "oppositeDirection" : true, "depth" : 44.82 * mm, "hasSecondDirection" : true, "secondDirectionOppositeDirection" : true, "secondDirectionDepth" : 25.57 * mm});
        }
        {
            var Q0;
            Q0=qCreatedBy(makeId("Front.planeOp"),FACE);
            var sketch = newSketch(context, id + "F37", { "sketchPlane" : qUnion([Q0])});
            skLineSegment(sketch, "E102.bottom", {"start": v(82.17, -43.31) * mm, "end": v(98.27, -43.31) * mm});
            skLineSegment(sketch, "E102.top", {"start": v(82.17, -52.61) * mm, "end": v(98.27, -52.61) * mm});
            skLineSegment(sketch, "E102.left", {"start": v(82.17, -43.31) * mm, "end": v(82.17, -52.61) * mm});
            skLineSegment(sketch, "E102.right", {"start": v(98.27, -43.31) * mm, "end": v(98.27, -52.61) * mm});
            skSolve(sketch);
        }
        {
            var Q0;
            Q0 = qSketchRegion(id + "F37", true);
            extrude(context, id + "F38", {"entities" : qUnion([Q0]), "operationType" : NewBodyOperationType.ADD, "depth" : 25.4 * mm, "hasSecondDirection" : true, "secondDirectionOppositeDirection" : false, "secondDirectionDepth" : 9.5 * mm});
        }
        {
            var Q0;
            Q0=qCreatedBy(makeId("Top.planeOp"),FACE);
            var sketch = newSketch(context, id + "F39", { "sketchPlane" : qUnion([Q0])});
            skCircle(sketch, "E103", {"center": v(85.28, -21.16) * mm, "radius": 2.19 * mm});
            skCircle(sketch, "E104", {"center": v(93.2, -20.96) * mm, "radius": 2.28 * mm});
            skSolve(sketch);
        }
        {
            var Q0;
            Q0 = qSketchRegion(id + "F39", true);
            extrude(context, id + "F40", {"entities" : qUnion([Q0]), "operationType" : NewBodyOperationType.REMOVE, "depth" : 25.4 * mm, "hasSecondDirection" : true, "secondDirectionOppositeDirection" : true, "secondDirectionDepth" : 80.47 * mm});
        }
        {
            var Q0;
            Q0=qCreatedBy(makeId("Right.planeOp"),FACE);
            var sketch = newSketch(context, id + "F41", { "sketchPlane" : qUnion([Q0])});
            skLineSegment(sketch, "E105", {"start": v(12.98, -2.18) * mm, "end": v(25.98, 17.53) * mm});
            skArc(sketch, "E106", {"start": v(12.98, 17.53) * mm, "mid": v(19.48, 15.62) * mm, "end": v(25.98, 17.53) * mm});
            skLineSegment(sketch, "E107", {"start": v(12.98, 17.53) * mm, "end": v(12.98, -2.18) * mm});
            skSolve(sketch);
        }
        {
            var Q0;
            Q0 = qSketchRegion(id + "F41", true);
            extrude(context, id + "F42", {"entities" : qUnion([Q0]), "operationType" : NewBodyOperationType.ADD, "depth" : 266.06 * mm, "hasSecondDirection" : true, "secondDirectionOppositeDirection" : false, "secondDirectionDepth" : 247.6 * mm});
        }
    });
